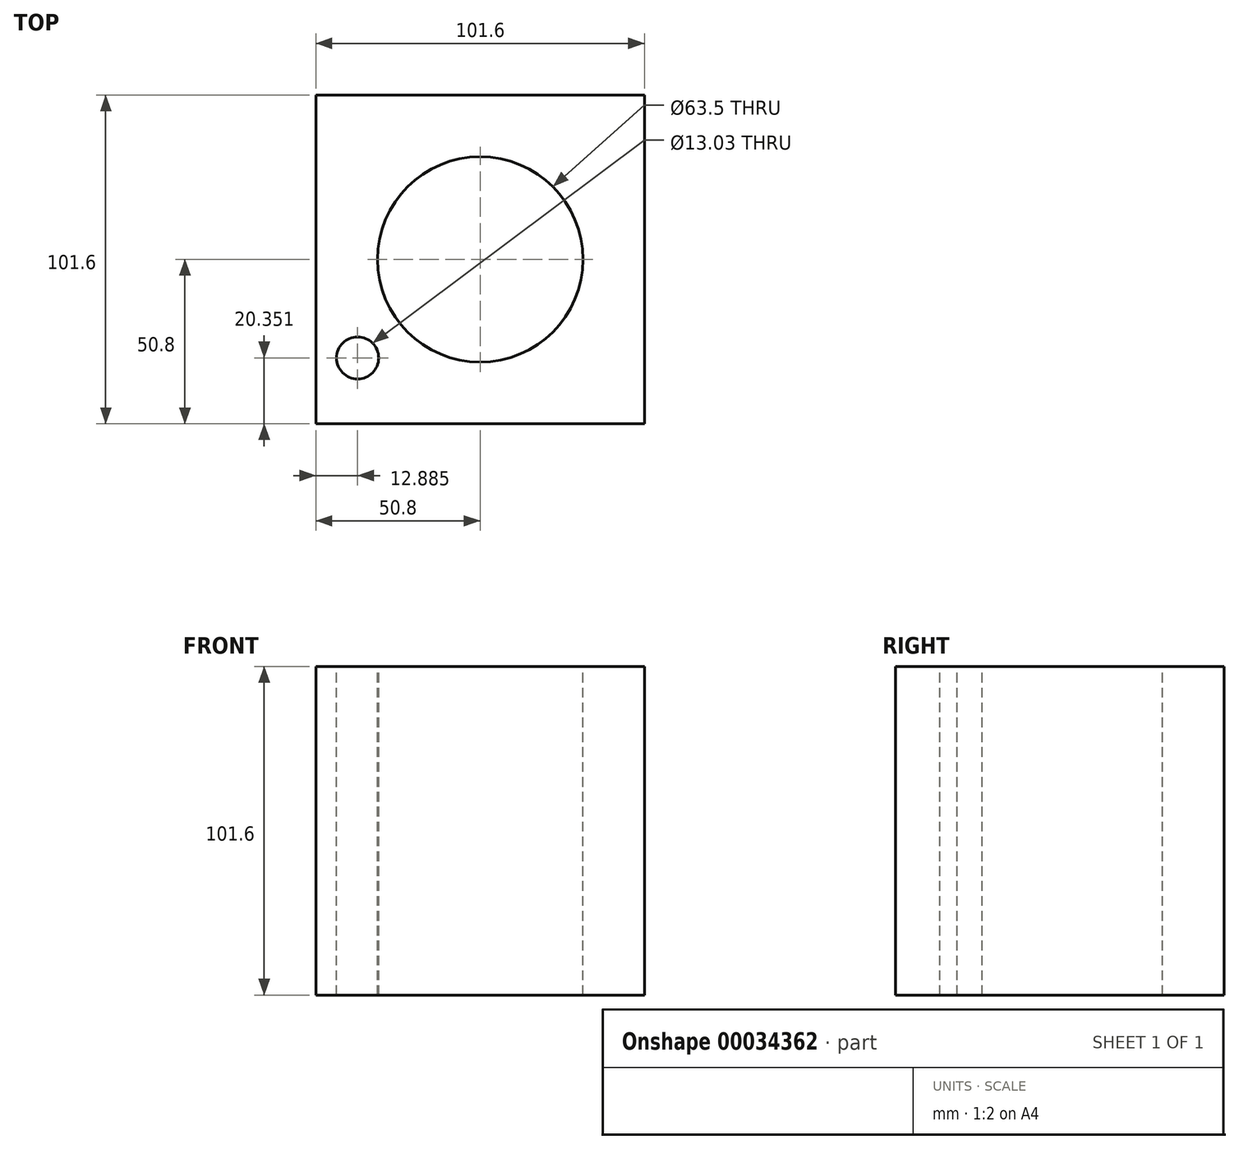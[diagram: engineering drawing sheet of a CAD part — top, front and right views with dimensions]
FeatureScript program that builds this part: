
annotation { "Feature Type Name" : "Feature", "Feature Type Description" : "" }
export const myFeature = defineFeature(function(context is Context, id is Id, definition is map)
    precondition{}
    {
        {
            var Q0;
            Q0=qCreatedBy(makeId("Front.planeOp"),FACE);
            var sketch = newSketch(context, id + "F0", { "sketchPlane" : qUnion([Q0])});
            skLineSegment(sketch, "E0.rect.bottom", {"start": v(-50.8, 50.8) * mm, "end": v(50.8, 50.8) * mm});
            skLineSegment(sketch, "E0.rect.top", {"start": v(-50.8, -50.8) * mm, "end": v(50.8, -50.8) * mm});
            skLineSegment(sketch, "E0.rect.left", {"start": v(-50.8, 50.8) * mm, "end": v(-50.8, -50.8) * mm});
            skLineSegment(sketch, "E0.rect.right", {"start": v(50.8, 50.8) * mm, "end": v(50.8, -50.8) * mm});
            skPoint(sketch, "E0.rect.middle", {"position": v(0, 0) * mm});
            skSolve(sketch);
        }
        {
            var Q0;
            Q0 = qSketchRegion(id + "F0", true);
            extrude(context, id + "F1", {"entities" : qUnion([Q0]), "endBound" : BoundingType.SYMMETRIC, "depth" : 101.6 * mm});
        }
        {
            var Q0;
            Q0=makeQuery(id+"F1.opExtrude","SWEPT_FACE",FACE,{"disambiguationData":[OSD([sQuery(id+"F0.wireOp",EDGE,"E0.rect.bottom")])]});
            var sketch = newSketch(context, id + "F2", { "sketchPlane" : qUnion([Q0])});
            skCircle(sketch, "E1", {"center": v(0, 0) * mm, "radius": 31.75 * mm});
            skSolve(sketch);
        }
        {
            var Q0;
            Q0 = qSketchRegion(id + "F2", true);
            extrude(context, id + "F3", {"entities" : qUnion([Q0]), "operationType" : NewBodyOperationType.REMOVE, "endBound" : BoundingType.THROUGH_ALL, "oppositeDirection" : true, "depth" : 25.4 * mm});
        }
        {
            var Q0;
            Q0=makeQuery(id+"F1.opExtrude","SWEPT_FACE",FACE,{"disambiguationData":[OSD([sQuery(id+"F0.wireOp",EDGE,"E0.rect.bottom")])]});
            var sketch = newSketch(context, id + "F4", { "sketchPlane" : qUnion([Q0])});
            skCircle(sketch, "E2", {"center": v(-37.91, -30.45) * mm, "radius": 6.52 * mm});
            skSolve(sketch);
        }
        {
            var Q0;
            Q0 = qSketchRegion(id + "F4", true);
            extrude(context, id + "F5", {"entities" : qUnion([Q0]), "operationType" : NewBodyOperationType.REMOVE, "endBound" : BoundingType.THROUGH_ALL, "oppositeDirection" : true, "depth" : 25.4 * mm});
        }
    });
